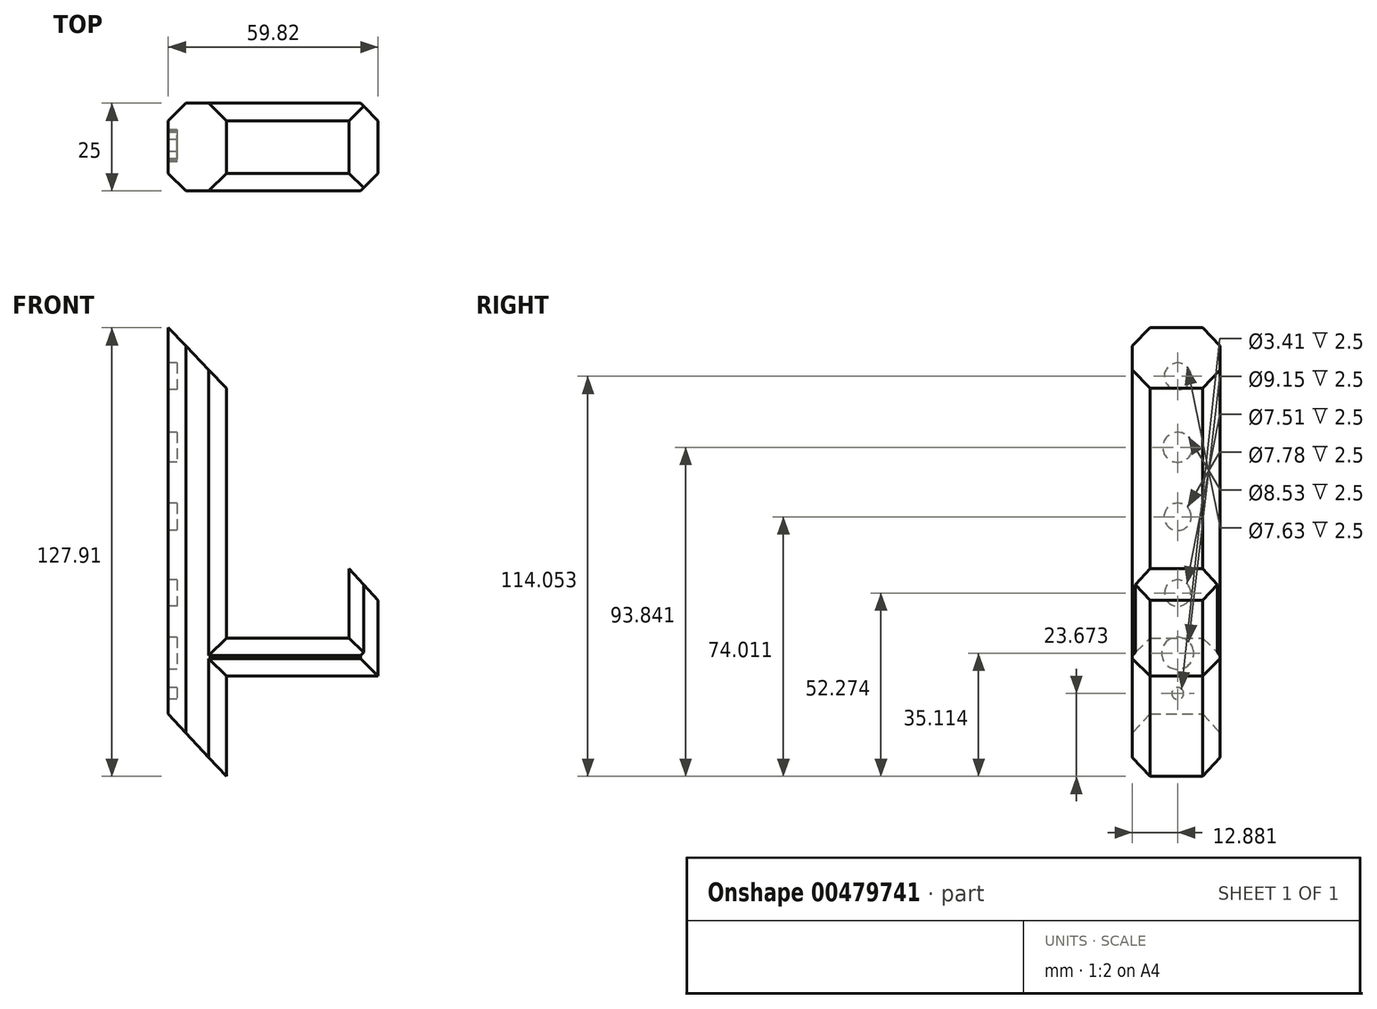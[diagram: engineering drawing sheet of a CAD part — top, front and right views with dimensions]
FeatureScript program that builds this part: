
annotation { "Feature Type Name" : "Feature", "Feature Type Description" : "" }
export const myFeature = defineFeature(function(context is Context, id is Id, definition is map)
    precondition{}
    {
        {
            var Q0;
            Q0=qCreatedBy(makeId("Front.planeOp"),FACE);
            var sketch = newSketch(context, id + "F0", { "sketchPlane" : qUnion([Q0])});
            skLineSegment(sketch, "E0", {"start": v(0, 21.64) * mm, "end": v(0, 0) * mm});
            skLineSegment(sketch, "E1", {"start": v(0, 0) * mm, "end": v(-43.27, 0) * mm});
            skLineSegment(sketch, "E2", {"start": v(-43.27, 0) * mm, "end": v(-43.27, 82.1) * mm});
            skLineSegment(sketch, "E3", {"start": v(-43.27, 82.1) * mm, "end": v(-59.82, 99.27) * mm});
            skLineSegment(sketch, "E4", {"start": v(-59.82, 99.27) * mm, "end": v(-59.82, -10.82) * mm});
            skLineSegment(sketch, "E5", {"start": v(-59.82, -10.82) * mm, "end": v(-43.27, -28.64) * mm});
            skLineSegment(sketch, "E6", {"start": v(-43.27, -28.64) * mm, "end": v(-43.27, 0) * mm});
            skLineSegment(sketch, "E7", {"start": v(0, 21.64) * mm, "end": v(-8.27, 30.55) * mm});
            skLineSegment(sketch, "E8", {"start": v(-8.27, 30.55) * mm, "end": v(-8.27, 10.82) * mm});
            skLineSegment(sketch, "E9", {"start": v(-8.27, 10.82) * mm, "end": v(-43.27, 10.82) * mm});
            skSolve(sketch);
        }
        {
            var Q0;
            Q0 = qSketchRegion(id + "F0", true);
            extrude(context, id + "F1", {"entities" : qUnion([Q0]), "depth" : 25 * mm});
        }
        {
            var Q0;
            Q0=makeQuery(id+"F1.opExtrude","CAP_EDGE",EDGE,{"disambiguationData":[OSD([sQuery(id+"F0.wireOp",EDGE,"E9")])],"isStart":false});
            var Q1;
            Q1=makeQuery(id+"F1.opExtrude","CAP_EDGE",EDGE,{"disambiguationData":[OSD([sQuery(id+"F0.wireOp",EDGE,"E1")])],"isStart":false});
            chamfer(context, id + "F2", {"entities" : qUnion([Q0, Q1]), "width" : 5 * mm, "tangentPropagation" : true});
        }
        {
            var Q0;
            Q0=makeQuery(id+"F1.opExtrude","CAP_EDGE",EDGE,{"disambiguationData":[OSD([sQuery(id+"F0.wireOp",EDGE,"E9")])],"isStart":true});
            var Q1;
            Q1=makeQuery(id+"F1.opExtrude","CAP_EDGE",EDGE,{"disambiguationData":[OSD([sQuery(id+"F0.wireOp",EDGE,"E1")])],"isStart":true});
            chamfer(context, id + "F3", {"entities" : qUnion([Q0, Q1]), "width" : 5 * mm, "tangentPropagation" : true});
        }
        {
            var Q0;
            Q0=makeQuery(id+"F1.opExtrude","CAP_EDGE",EDGE,{"disambiguationData":[OSD([sQuery(id+"F0.wireOp",EDGE,"E0")])],"isStart":false});
            var Q1;
            Q1=makeQuery(id+"F1.opExtrude","CAP_EDGE",EDGE,{"disambiguationData":[OSD([sQuery(id+"F0.wireOp",EDGE,"E8")])],"isStart":false});
            var Q2;
            Q2=makeQuery(id+"F1.opExtrude","CAP_EDGE",EDGE,{"disambiguationData":[OSD([sQuery(id+"F0.wireOp",EDGE,"E0")])],"isStart":true});
            var Q3;
            Q3=makeQuery(id+"F1.opExtrude","CAP_EDGE",EDGE,{"disambiguationData":[OSD([sQuery(id+"F0.wireOp",EDGE,"E8")])],"isStart":true});
            chamfer(context, id + "F4", {"entities" : qUnion([Q0, Q1, Q2, Q3]), "width" : 5 * mm, "tangentPropagation" : true});
        }
        {
            var Q0;
            Q0=makeQuery(id+"F1.opExtrude","CAP_EDGE",EDGE,{"disambiguationData":[OSD([sQuery(id+"F0.wireOp",EDGE,"E2")])],"isStart":true});
            var Q1;
            Q1=makeQuery(id+"F1.opExtrude","CAP_EDGE",EDGE,{"disambiguationData":[OSD([sQuery(id+"F0.wireOp",EDGE,"E6")])],"isStart":true});
            var Q2;
            Q2=makeQuery(id+"F1.opExtrude","CAP_EDGE",EDGE,{"disambiguationData":[OSD([sQuery(id+"F0.wireOp",EDGE,"E4")])],"isStart":true});
            var Q3;
            Q3=makeQuery(id+"F1.opExtrude","CAP_EDGE",EDGE,{"disambiguationData":[OSD([sQuery(id+"F0.wireOp",EDGE,"E2")])],"isStart":false});
            var Q4;
            Q4=makeQuery(id+"F1.opExtrude","CAP_EDGE",EDGE,{"disambiguationData":[OSD([sQuery(id+"F0.wireOp",EDGE,"E6")])],"isStart":false});
            var Q5;
            Q5=makeQuery(id+"F1.opExtrude","CAP_EDGE",EDGE,{"disambiguationData":[OSD([sQuery(id+"F0.wireOp",EDGE,"E4")])],"isStart":false});
            chamfer(context, id + "F5", {"entities" : qUnion([Q0, Q1, Q2, Q3, Q4, Q5]), "width" : 5 * mm, "tangentPropagation" : true});
        }
        {
            var Q0;
            Q0=makeQuery(id+"F1.opExtrude","SWEPT_FACE",FACE,{"disambiguationData":[OSD([sQuery(id+"F0.wireOp",EDGE,"E4")])]});
            var sketch = newSketch(context, id + "F6", { "sketchPlane" : qUnion([Q0])});
            skCircle(sketch, "E10", {"center": v(12.12, 85.41) * mm, "radius": 3.81 * mm});
            skCircle(sketch, "E11", {"center": v(12.12, 65.2) * mm, "radius": 4.26 * mm});
            skCircle(sketch, "E12", {"center": v(12.12, 45.37) * mm, "radius": 3.89 * mm});
            skCircle(sketch, "E13", {"center": v(12.12, 23.63) * mm, "radius": 3.76 * mm});
            skCircle(sketch, "E14", {"center": v(12.12, 6.47) * mm, "radius": 4.58 * mm});
            skCircle(sketch, "E15", {"center": v(12.12, -4.97) * mm, "radius": 1.7 * mm});
            skSolve(sketch);
        }
        {
            var Q0;
            Q0 = qSketchRegion(id + "F6", true);
            extrude(context, id + "F7", {"entities" : qUnion([Q0]), "operationType" : NewBodyOperationType.REMOVE, "oppositeDirection" : true, "depth" : 2.5 * mm});
        }
    });
